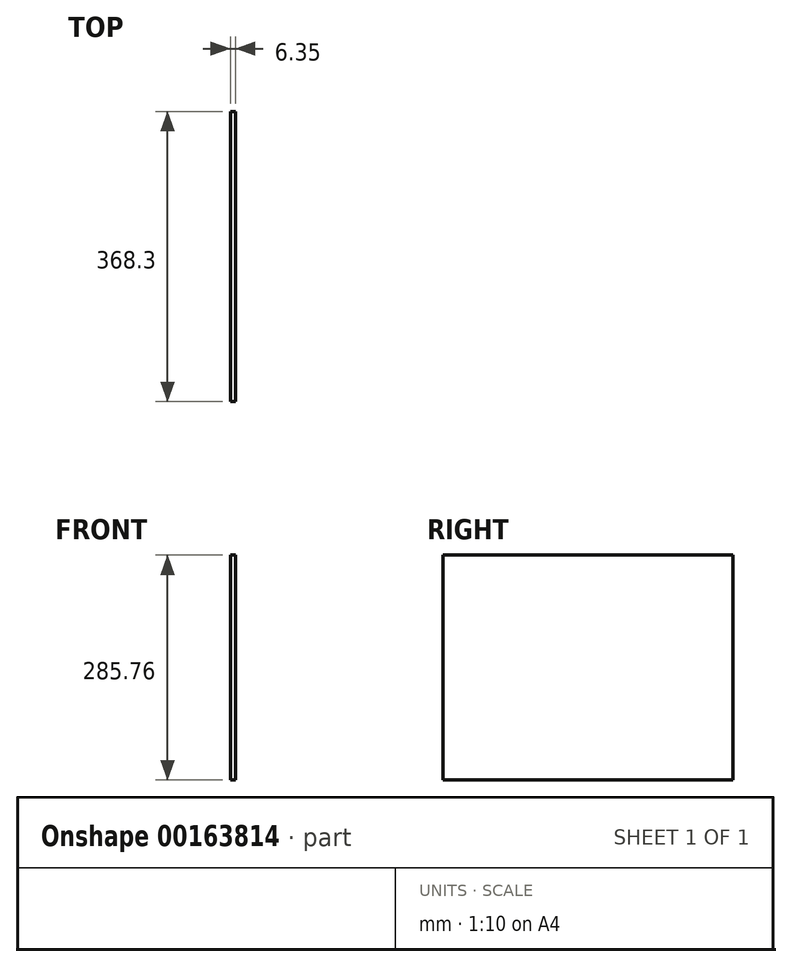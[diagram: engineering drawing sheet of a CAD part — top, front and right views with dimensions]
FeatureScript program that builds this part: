
annotation { "Feature Type Name" : "Feature", "Feature Type Description" : "" }
export const myFeature = defineFeature(function(context is Context, id is Id, definition is map)
    precondition{}
    {
        {
            var Q0;
            Q0=qCreatedBy(makeId("Right.planeOp"),FACE);
            var sketch = newSketch(context, id + "F0", { "sketchPlane" : qUnion([Q0])});
            skLineSegment(sketch, "E0.bottom", {"start": v(184.15, -142.88) * mm, "end": v(-184.15, -142.88) * mm});
            skLineSegment(sketch, "E0.top", {"start": v(184.15, 142.88) * mm, "end": v(-184.15, 142.87) * mm});
            skLineSegment(sketch, "E0.left", {"start": v(184.15, -142.88) * mm, "end": v(184.15, 142.88) * mm});
            skLineSegment(sketch, "E0.right", {"start": v(-184.15, -142.88) * mm, "end": v(-184.15, 142.87) * mm});
            skPoint(sketch, "E0.middle", {"position": v(0, 0) * mm});
            skSolve(sketch);
        }
        {
            var Q0;
            Q0=qSketchRegion(id+"F0",true);
            extrude(context, id + "F1", {"entities" : qUnion([Q0]), "depth" : 6.35 * mm});
        }
    });
